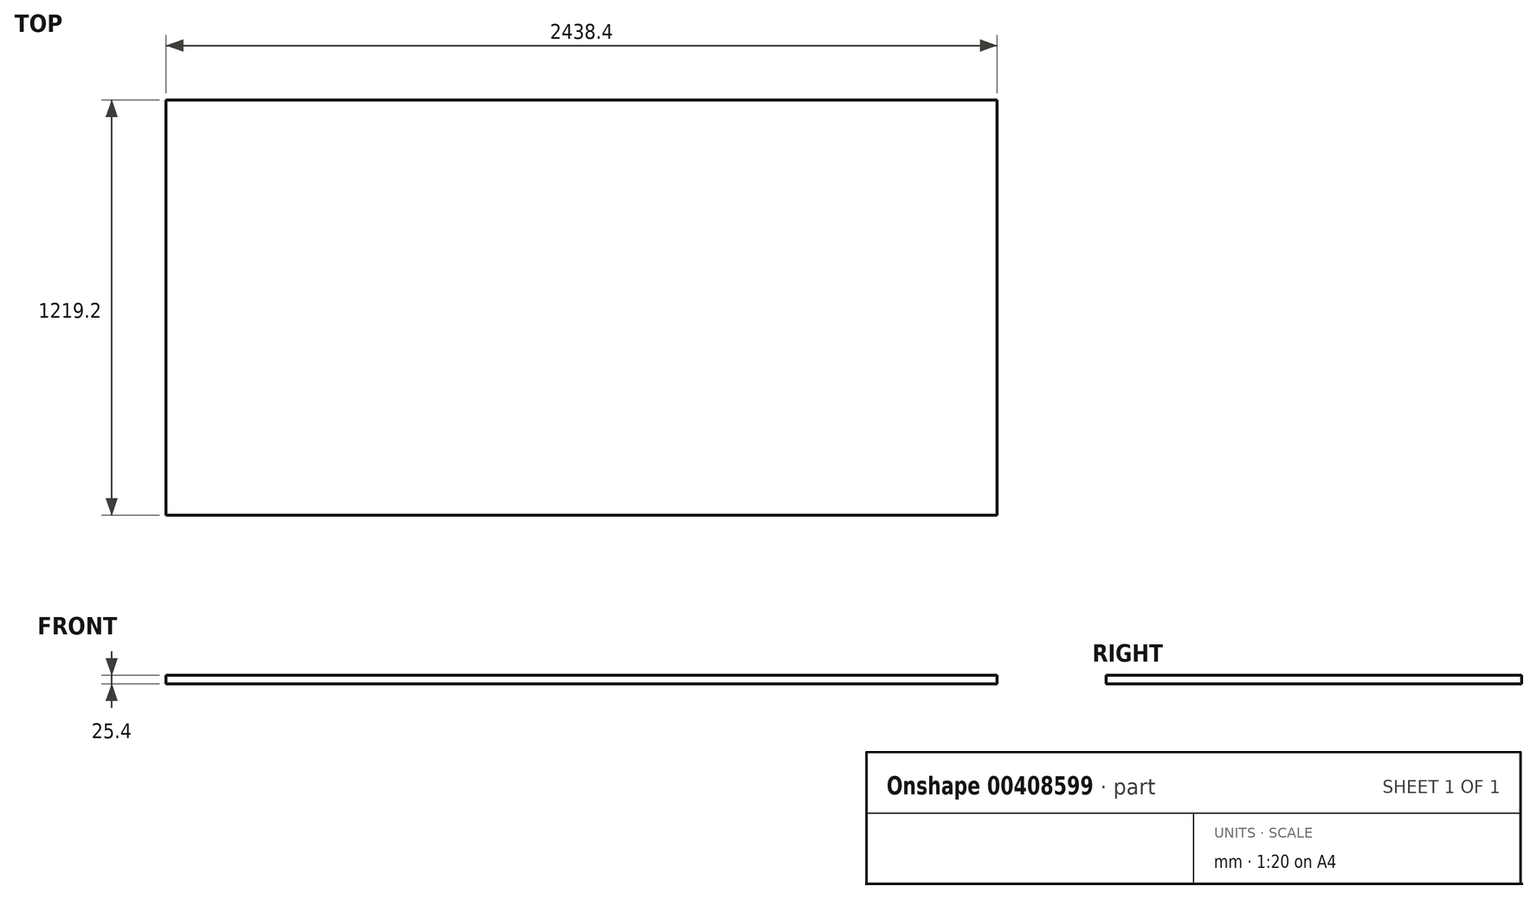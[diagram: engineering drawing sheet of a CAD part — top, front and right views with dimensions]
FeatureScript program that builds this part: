
annotation { "Feature Type Name" : "Feature", "Feature Type Description" : "" }
export const myFeature = defineFeature(function(context is Context, id is Id, definition is map)
    precondition{}
    {
        {
            var Q0;
            Q0=qCreatedBy(makeId("Top.planeOp"),FACE);
            var sketch = newSketch(context, id + "F0", { "sketchPlane" : qUnion([Q0])});
            skLineSegment(sketch, "E0.bottom", {"start": v(-1244.2, -526.16) * mm, "end": v(1194.2, -526.16) * mm});
            skLineSegment(sketch, "E0.top", {"start": v(-1244.2, 693.04) * mm, "end": v(1194.2, 693.04) * mm});
            skLineSegment(sketch, "E0.left", {"start": v(-1244.2, -526.16) * mm, "end": v(-1244.2, 693.04) * mm});
            skLineSegment(sketch, "E0.right", {"start": v(1194.2, -526.16) * mm, "end": v(1194.2, 693.04) * mm});
            skSolve(sketch);
        }
        {
            var Q0;
            Q0=makeQuery(id+"F0.imprint","IMPRINT",FACE,{"disambiguationData":[TD([[makeQuery(id+"F0.imprint","IMPRINT",EDGE,{"derivedFrom":sQuery(id+"F0.wireOp",EDGE,"E0.bottom")}),1.0]])]});
            extrude(context, id + "F1", {"entities" : qUnion([Q0]), "oppositeDirection" : true, "depth" : 25.4 * mm, "offsetDistance" : 25.4 * mm});
        }
    });
